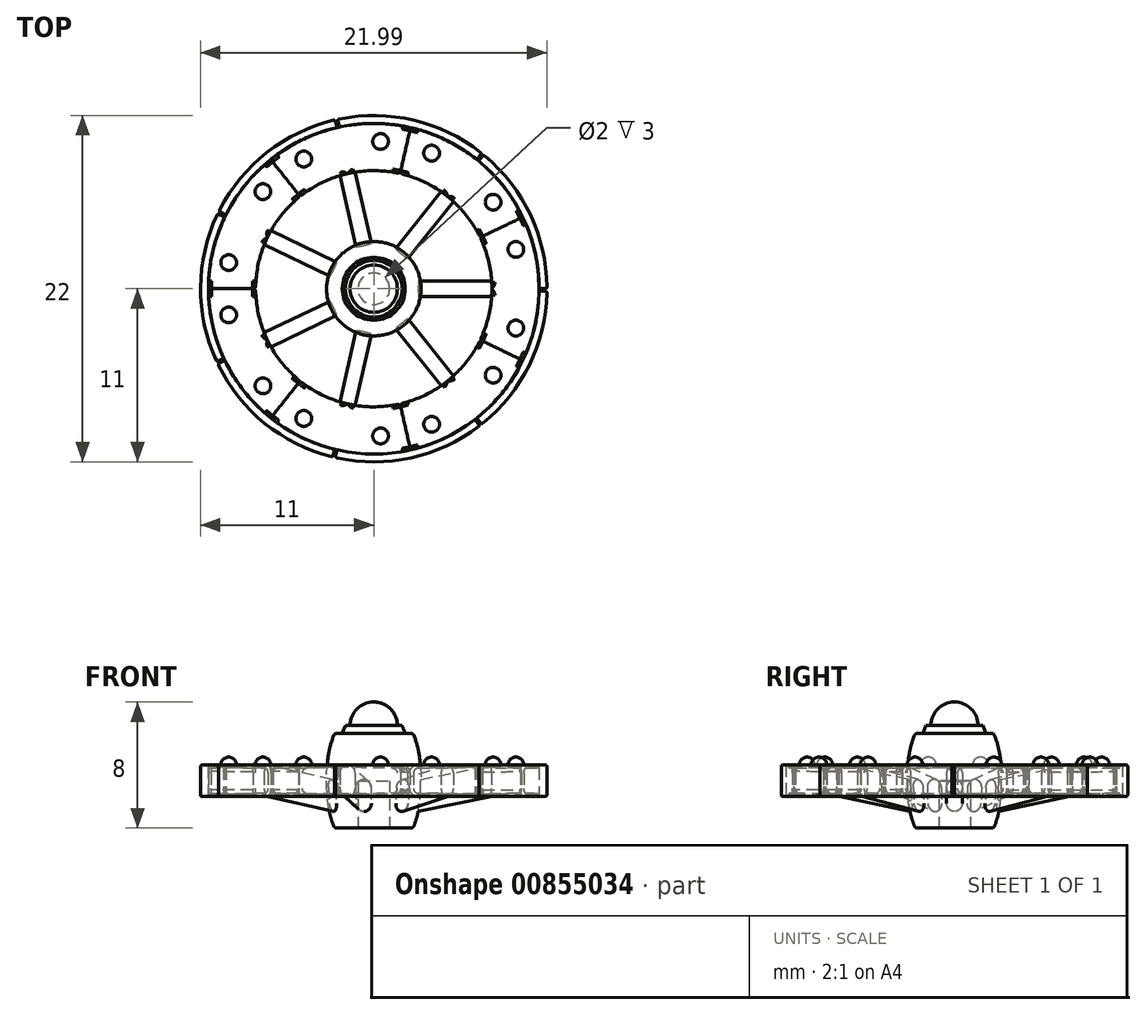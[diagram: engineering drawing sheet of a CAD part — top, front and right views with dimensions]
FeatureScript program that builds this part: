
annotation { "Feature Type Name" : "Feature", "Feature Type Description" : "" }
export const myFeature = defineFeature(function(context is Context, id is Id, definition is map)
    precondition{}
    {
        {
            var Q0;
            Q0=qCreatedBy(makeId("Front.planeOp"),FACE);
            var sketch = newSketch(context, id + "F0", { "sketchPlane" : qUnion([Q0])});
            skLineSegment(sketch, "E0", {"start": v(0, 3) * mm, "end": v(2.5, 3) * mm});
            skLineSegment(sketch, "E1", {"start": v(0, -3) * mm, "end": v(2.5, -3) * mm});
            skFitSpline(sketch, "E2", {"points": [v(2.5, 3) * mm, v(3, 0) * mm, v(2.5, -3) * mm], "startDerivative": vector(2.5, -6) * mm, "endDerivative": vector(-2.5, -6) * mm});
            skLineSegment(sketch, "E3", {"start": v(0, 3) * mm, "end": v(0, -3) * mm});
            skSolve(sketch);
        }
        {
            var Q0;
            Q0=makeQuery(id+"F0.imprint","IMPRINT",FACE,{"disambiguationData":[TD([[makeQuery(id+"F0.imprint","IMPRINT",EDGE,{"derivedFrom":sQuery(id+"F0.wireOp",EDGE,"E0")}),-1.0]])]});
            var Q1;
            Q1=sQuery(id+"F0.wireOp",EDGE,"E3");
            revolve(context, id + "F1", {"surfaceOperationType" : NewSurfaceOperationType.NEW, "entities" : qUnion([Q0]), "axis" : qUnion([Q1]), "revolveType" : RevolveType.SYMMETRIC, "angle" : 51.5 * degree});
        }
        {
            var Q0;
            Q0=qCreatedBy(makeId("Front.planeOp"),FACE);
            var sketch = newSketch(context, id + "F2", { "sketchPlane" : qUnion([Q0])});
            skLineSegment(sketch, "E4", {"start": v(2.6, -2) * mm, "end": v(7.5, -1) * mm});
            skLineSegment(sketch, "E5", {"start": v(7.5, -1) * mm, "end": v(10.5, -1) * mm});
            skLineSegment(sketch, "E6", {"start": v(10.5, -1) * mm, "end": v(10.5, 1) * mm});
            skLineSegment(sketch, "E7", {"start": v(10.5, 1) * mm, "end": v(7.5, 1) * mm});
            skLineSegment(sketch, "E8", {"start": v(7.5, 1) * mm, "end": v(2.6, 0) * mm});
            skPoint(sketch, "E9.0", {"position": v(2.5, -3) * mm});
            skFitSpline(sketch, "E10.0", {"points": [v(2.5, 3) * mm, v(2.92, 2) * mm, v(3.08, 0) * mm, v(2.92, -2) * mm, v(2.5, -3) * mm]});
            skLineSegment(sketch, "E11", {"start": v(7.5, 1) * mm, "end": v(7.5, -1) * mm});
            skLineSegment(sketch, "E12", {"start": v(2.6, 0) * mm, "end": v(2.6, -2) * mm});
            skSolve(sketch);
        }
        {
            var Q0;
            {var subQ0=sQuery(id+"F2.wireOp",EDGE,"E12");Q0=makeQuery(id+"F2.imprint","IMPRINT",FACE,{"disambiguationData":[TD([[makeQuery(id+"F2.imprint","IMPRINT",EDGE,{"derivedFrom":subQ0}),1.0]])]});}
            var Q1;
            {var subQ0=sQuery(id+"F2.wireOp",EDGE,"E11");Q1=makeQuery(id+"F2.imprint","IMPRINT",FACE,{"disambiguationData":[TD([[makeQuery(id+"F2.imprint","IMPRINT",EDGE,{"derivedFrom":subQ0}),-1.0]])]});}
            extrude(context, id + "F3", {"entities" : qUnion([Q0, Q1]), "operationType" : NewBodyOperationType.ADD, "endBound" : BoundingType.SYMMETRIC, "depth" : 1 * mm, "offsetDistance" : 25 * mm});
        }
        {
            var Q0;
            Q0=qCreatedBy(makeId("Top.planeOp"),FACE);
            var sketch = newSketch(context, id + "F4", { "sketchPlane" : qUnion([Q0])});
            skPoint(sketch, "E13.0", {"position": v(7.5, 0) * mm});
            skCircle(sketch, "E14", {"center": v(0, 0) * mm, "radius": 7.5 * mm});
            skCircle(sketch, "E15", {"center": v(0, 0) * mm, "radius": 10.5 * mm});
            skLineSegment(sketch, "E16", {"start": v(0, 0) * mm, "end": v(9.46, 4.56) * mm});
            skLineSegment(sketch, "E17", {"start": v(0, 0) * mm, "end": v(9.46, -4.56) * mm});
            skLineSegment(sketch, "E18", {"start": v(7.5, 0) * mm, "end": v(9.46, 4.56) * mm, "construction": true});
            skLineSegment(sketch, "E19", {"start": v(7.5, 0) * mm, "end": v(9.46, -4.56) * mm, "construction": true});
            skSolve(sketch);
        }
        {
            var Q0;
            {var subQ0=sQuery(id+"F4.wireOp",EDGE,"E16");var subQ1=sQuery(id+"F4.wireOp",EDGE,"E14");var subQ2=makeQuery(id+"F4.imprint","INTERSECT",VERTEX,{"derivedFrom":[subQ1,subQ0]});Q0=makeQuery(id+"F4.imprint","IMPRINT",FACE,{"disambiguationData":[TD([[makeQuery(id+"F4.imprint","IMPRINT",EDGE,{"disambiguationData":[TD([[subQ2,1.0]])],"derivedFrom":subQ1}),-1.0]])]});}
            extrude(context, id + "F5", {"entities" : qUnion([Q0]), "operationType" : NewBodyOperationType.ADD, "endBound" : BoundingType.SYMMETRIC, "depth" : 2 * mm, "offsetDistance" : 25 * mm});
        }
        {
            var Q0;
            Q0=makeQuery(id+"F5.opExtrude","CAP_EDGE",EDGE,{"disambiguationData":[OSD([sQuery(id+"F4.wireOp",EDGE,"E17")])],"isStart":false});
            var Q1;
            Q1=makeQuery(id+"F5.opExtrude","CAP_EDGE",EDGE,{"disambiguationData":[OSD([sQuery(id+"F4.wireOp",EDGE,"E17")])],"isStart":true});
            var Q2;
            Q2=makeQuery(id+"F5.opExtrude","CAP_EDGE",EDGE,{"disambiguationData":[OSD([sQuery(id+"F4.wireOp",EDGE,"E16")])],"isStart":false});
            var Q3;
            Q3=makeQuery(id+"F5.opExtrude","CAP_EDGE",EDGE,{"disambiguationData":[OSD([sQuery(id+"F4.wireOp",EDGE,"E16")])],"isStart":true});
            var Q4;
            Q4=makeQuery(id+"F3.opExtrude","CAP_EDGE",EDGE,{"disambiguationData":[OSD([sQuery(id+"F2.wireOp",EDGE,"E4")])],"isStart":false});
            var Q5;
            Q5=makeQuery(id+"F3.opExtrude","CAP_EDGE",EDGE,{"disambiguationData":[OSD([sQuery(id+"F2.wireOp",EDGE,"E4")])],"isStart":true});
            var Q6;
            Q6=makeQuery(id+"F3.opExtrude","CAP_EDGE",EDGE,{"disambiguationData":[OSD([sQuery(id+"F2.wireOp",EDGE,"E8")])],"isStart":false});
            var Q7;
            Q7=makeQuery(id+"F3.opExtrude","CAP_EDGE",EDGE,{"disambiguationData":[OSD([sQuery(id+"F2.wireOp",EDGE,"E8")])],"isStart":true});
            fillet(context, id + "F6", {"entities" : qUnion([Q0, Q1, Q2, Q3, Q4, Q5, Q6, Q7]), "radius" : .5 * mm, "tangentPropagation" : true, "allowEdgeOverflow" : false});
        }
        {
            var Q0;
            {var subQ0=sQuery(id+"F4.wireOp",EDGE,"E14");var subQ1=sQuery(id+"F4.wireOp",EDGE,"E16");Q0=makeQuery(id+"F5.boolean.opBoolean","SPLIT",EDGE,{"disambiguationData":[TD([makeQuery(id+"F5.opExtrude","SWEPT_FACE",FACE,{"disambiguationData":[OSD([subQ1])]})])],"derivedFrom":makeQuery(id+"F5.opExtrude","CAP_EDGE",EDGE,{"disambiguationData":[OSD([subQ0])],"isStart":false})});}
            var Q1;
            Q1=makeQuery(id+"F5.opExtrude","CAP_EDGE",EDGE,{"disambiguationData":[OSD([sQuery(id+"F4.wireOp",EDGE,"E15")])],"isStart":false});
            var Q2;
            Q2=makeQuery(id+"F1.opRevolve","SWEPT_EDGE",EDGE,{"disambiguationData":[OSD([sQuery(id+"F0.wireOp",EDGE,"E0"),sQuery(id+"F0.wireOp",EDGE,"E2")])]});
            var Q3;
            Q3=makeQuery(id+"F1.opRevolve","SWEPT_EDGE",EDGE,{"disambiguationData":[OSD([sQuery(id+"F0.wireOp",EDGE,"E1"),sQuery(id+"F0.wireOp",EDGE,"E2")])]});
            fillet(context, id + "F7", {"entities" : qUnion([Q0, Q1, Q2, Q3]), "radius" : .2 * mm, "tangentPropagation" : true, "allowEdgeOverflow" : false});
        }
        {
            var Q0;
            Q0=makeQuery(id+"F5.opExtrude","CAP_FACE",FACE,{"disambiguationData":[OSD([sQuery(id+"F4.wireOp",EDGE,"E14"),sQuery(id+"F4.wireOp",EDGE,"E15"),sQuery(id+"F4.wireOp",EDGE,"E16"),sQuery(id+"F4.wireOp",EDGE,"E17")])],"isStart":false});
            var sketch = newSketch(context, id + "F8", { "sketchPlane" : qUnion([Q0])});
            skCircle(sketch, "E20", {"center": v(9.02, 2.5) * mm, "radius": 0.5 * mm});
            skCircle(sketch, "E21", {"center": v(9.02, -2.5) * mm, "radius": 0.5 * mm});
            skArc(sketch, "E22", {"start": v(8.58, -3.58) * mm, "mid": v(9.42, 0) * mm, "end": v(8.58, 3.58) * mm});
            skSolve(sketch);
        }
        {
            var Q0;
            {var subQ0=sQuery(id+"F8.wireOp",EDGE,"E22");var subQ1=sQuery(id+"F8.wireOp",EDGE,"E20");var subQ2=makeQuery(id+"F8.imprint","INTERSECT",VERTEX,{"disambiguationData":[OD(0.0)],"derivedFrom":[subQ1,subQ0]});Q0=makeQuery(id+"F8.imprint","IMPRINT",FACE,{"disambiguationData":[TD([[makeQuery(id+"F8.imprint","IMPRINT",EDGE,{"disambiguationData":[TD([[subQ2,-1.0]])],"derivedFrom":subQ1}),1.0]])]});}
            var Q1;
            {var subQ0=sQuery(id+"F8.wireOp",EDGE,"E22");var subQ1=sQuery(id+"F8.wireOp",EDGE,"E20");var subQ2=makeQuery(id+"F8.imprint","INTERSECT",VERTEX,{"disambiguationData":[OD(0.0)],"derivedFrom":[subQ1,subQ0]});Q1=makeQuery(id+"F8.imprint","IMPRINT",FACE,{"disambiguationData":[TD([[makeQuery(id+"F8.imprint","IMPRINT",EDGE,{"disambiguationData":[TD([[subQ2,1.0]])],"derivedFrom":subQ1}),1.0]])]});}
            var Q2;
            {var subQ0=sQuery(id+"F8.wireOp",EDGE,"E22");var subQ1=sQuery(id+"F8.wireOp",EDGE,"E21");var subQ2=makeQuery(id+"F8.imprint","INTERSECT",VERTEX,{"disambiguationData":[OD(0.0)],"derivedFrom":[subQ1,subQ0]});Q2=makeQuery(id+"F8.imprint","IMPRINT",FACE,{"disambiguationData":[TD([[makeQuery(id+"F8.imprint","IMPRINT",EDGE,{"disambiguationData":[TD([[subQ2,-1.0]])],"derivedFrom":subQ1}),1.0]])]});}
            var Q3;
            {var subQ0=sQuery(id+"F8.wireOp",EDGE,"E22");var subQ1=sQuery(id+"F8.wireOp",EDGE,"E21");var subQ2=makeQuery(id+"F8.imprint","INTERSECT",VERTEX,{"disambiguationData":[OD(0.0)],"derivedFrom":[subQ1,subQ0]});Q3=makeQuery(id+"F8.imprint","IMPRINT",FACE,{"disambiguationData":[TD([[makeQuery(id+"F8.imprint","IMPRINT",EDGE,{"disambiguationData":[TD([[subQ2,1.0]])],"derivedFrom":subQ1}),1.0]])]});}
            extrude(context, id + "F9", {"entities" : qUnion([Q0, Q1, Q2, Q3]), "operationType" : NewBodyOperationType.ADD, "depth" : 0.5 * mm, "offsetDistance" : 25 * mm});
        }
        {
            var Q0;
            Q0=makeQuery(id+"F9.opExtrude","CAP_EDGE",EDGE,{"disambiguationData":[OSD([sQuery(id+"F8.wireOp",EDGE,"E20")])],"isStart":false});
            var Q1;
            Q1=makeQuery(id+"F9.opExtrude","CAP_EDGE",EDGE,{"disambiguationData":[OSD([sQuery(id+"F8.wireOp",EDGE,"E21")])],"isStart":false});
            fillet(context, id + "F10", {"entities" : qUnion([Q0, Q1]), "radius" : .5 * mm, "tangentPropagation" : true, "allowEdgeOverflow" : false});
        }
        {
            var Q0;
            Q0=makeQuery(id+"F3.opExtrude","SWEPT_BODY",BODY,{"disambiguationData":[OSD([sQuery(id+"F2.wireOp",EDGE,"E4"),sQuery(id+"F2.wireOp",EDGE,"E8"),sQuery(id+"F2.wireOp",EDGE,"E10.0"),sQuery(id+"F2.wireOp",EDGE,"E11")])]});
            var Q1;
            Q1=makeQuery(id+"F1.opRevolve","SWEPT_BODY",BODY,{"disambiguationData":[OSD([sQuery(id+"F0.wireOp",EDGE,"E0"),sQuery(id+"F0.wireOp",EDGE,"E1"),sQuery(id+"F0.wireOp",EDGE,"E2"),sQuery(id+"F0.wireOp",EDGE,"E3")])]});
            var Q2;
            Q2=sQuery(id+"F0.wireOp",EDGE,"E3");
            circularPattern(context, id + "F11", {"operationType" : NewBodyOperationType.ADD, "entities" : qUnion([Q0, Q1]), "axis" : qUnion([Q2]), "angle" : 360 * degree, "instanceCount" : 7, "equalSpace" : true});
        }
        {
            var Q0;
            Q0=makeQuery(id+"F5.opExtrude","CAP_FACE",FACE,{"disambiguationData":[OSD([sQuery(id+"F4.wireOp",EDGE,"E14"),sQuery(id+"F4.wireOp",EDGE,"E15"),sQuery(id+"F4.wireOp",EDGE,"E16"),sQuery(id+"F4.wireOp",EDGE,"E17")])],"isStart":false});
            var sketch = newSketch(context, id + "F12", { "sketchPlane" : qUnion([Q0])});
            skArc(sketch, "E23", {"start": v(10.5, 0) * mm, "mid": v(9.5, 4.49) * mm, "end": v(6.66, 8.1) * mm});
            skLineSegment(sketch, "E24", {"start": v(6.66, 8.1) * mm, "end": v(6.92, 8.42) * mm});
            skLineSegment(sketch, "E25", {"start": v(10.5, 0) * mm, "end": v(10.9, 0) * mm});
            skArc(sketch, "E26", {"start": v(11, 0.1) * mm, "mid": v(9.95, 4.7) * mm, "end": v(7.06, 8.43) * mm});
            skLineSegment(sketch, "E27", {"start": v(0, 0) * mm, "end": v(9.95, 4.7) * mm, "construction": true});
            skPoint(sketch, "E28.visualSharp", {"position": v(6.98, 8.5) * mm});
            skArc(sketch, "E28.filletArc", {"start": v(7.06, 8.43) * mm, "mid": v(6.99, 8.45) * mm, "end": v(6.92, 8.42) * mm});
            skPoint(sketch, "E29.visualSharp", {"position": v(11, 0) * mm});
            skArc(sketch, "E29.filletArc", {"start": v(10.9, 0) * mm, "mid": v(10.97, 0.03) * mm, "end": v(11, 0.1) * mm});
            skSolve(sketch);
        }
        {
            var Q0;
            Q0=makeQuery(id+"F12.imprint","IMPRINT",FACE,{"disambiguationData":[TD([[makeQuery(id+"F12.imprint","IMPRINT",EDGE,{"derivedFrom":sQuery(id+"F12.wireOp",EDGE,"E23")}),-1.0]])]});
            extrude(context, id + "F13", {"entities" : qUnion([Q0]), "oppositeDirection" : true, "depth" : 2 * mm, "offsetDistance" : 25 * mm});
        }
        {
            var Q0;
            Q0=makeQuery(id+"F13.opExtrude","CAP_EDGE",EDGE,{"disambiguationData":[OSD([sQuery(id+"F12.wireOp",EDGE,"E26")])],"isStart":true});
            var Q1;
            Q1=makeQuery(id+"F13.opExtrude","CAP_EDGE",EDGE,{"disambiguationData":[OSD([sQuery(id+"F12.wireOp",EDGE,"E26")])],"isStart":false});
            fillet(context, id + "F14", {"entities" : qUnion([Q0, Q1]), "radius" : .1 * mm, "tangentPropagation" : true, "allowEdgeOverflow" : false});
        }
        {
            var Q0;
            Q0=makeQuery(id+"F13.opExtrude","SWEPT_BODY",BODY,{"disambiguationData":[OSD([sQuery(id+"F12.wireOp",EDGE,"E23"),sQuery(id+"F12.wireOp",EDGE,"E24"),sQuery(id+"F12.wireOp",EDGE,"E25"),sQuery(id+"F12.wireOp",EDGE,"E26")])]});
            var Q1;
            Q1=sQuery(id+"F0.wireOp",EDGE,"E3");
            circularPattern(context, id + "F15", {"operationType" : NewBodyOperationType.ADD, "entities" : qUnion([Q0]), "axis" : qUnion([Q1]), "angle" : 360 * degree, "instanceCount" : 7, "equalSpace" : true});
        }
        {
            var Q0;
            Q0=makeQuery(id+"F1.opRevolve","SWEPT_FACE",FACE,{"disambiguationData":[OSD([sQuery(id+"F0.wireOp",EDGE,"E0")])]});
            var sketch = newSketch(context, id + "F16", { "sketchPlane" : qUnion([Q0])});
            skCircle(sketch, "E30", {"center": v(0, 0) * mm, "radius": 2 * mm});
            skSolve(sketch);
        }
        {
            var Q0;
            Q0=makeQuery(id+"F16.imprint","IMPRINT",FACE,{"disambiguationData":[TD([[makeQuery(id+"F16.imprint","IMPRINT",EDGE,{"derivedFrom":sQuery(id+"F16.wireOp",EDGE,"E30")}),1.0]])]});
            extrude(context, id + "F17", {"entities" : qUnion([Q0]), "operationType" : NewBodyOperationType.ADD, "depth" : .5 * mm, "offsetDistance" : 25 * mm});
        }
        {
            var Q0;
            Q0=makeQuery(id+"F17.opExtrude","CAP_EDGE",EDGE,{"disambiguationData":[OSD([sQuery(id+"F16.wireOp",EDGE,"E30")])],"isStart":false});
            chamfer(context, id + "F18", {"entities" : qUnion([Q0]), "chamferType" : ChamferType.TWO_OFFSETS, "width1" : 0.2 * mm, "oppositeDirection" : false, "width2" : .5 * mm, "tangentPropagation" : true});
        }
        {
            var Q0;
            Q0=makeQuery(id+"F17.opExtrude","CAP_FACE",FACE,{"disambiguationData":[OSD([sQuery(id+"F16.wireOp",EDGE,"E30")])],"isStart":false});
            var sketch = newSketch(context, id + "F19", { "sketchPlane" : qUnion([Q0])});
            skCircle(sketch, "E31", {"center": v(0, 0) * mm, "radius": 1.5 * mm});
            skSolve(sketch);
        }
        {
            var Q0;
            Q0=makeQuery(id+"F19.imprint","IMPRINT",FACE,{"disambiguationData":[TD([[makeQuery(id+"F19.imprint","IMPRINT",EDGE,{"derivedFrom":sQuery(id+"F19.wireOp",EDGE,"E31")}),1.0]])]});
            extrude(context, id + "F20", {"entities" : qUnion([Q0]), "operationType" : NewBodyOperationType.ADD, "depth" : 1.5 * mm, "offsetDistance" : 25 * mm});
        }
        {
            var Q0;
            Q0=makeQuery(id+"F20.opExtrude","CAP_EDGE",EDGE,{"disambiguationData":[OSD([sQuery(id+"F19.wireOp",EDGE,"E31")])],"isStart":false});
            fillet(context, id + "F21", {"entities" : qUnion([Q0]), "radius" : 1.5 * mm, "tangentPropagation" : true, "allowEdgeOverflow" : false});
        }
        {
            var Q0;
            Q0=makeQuery(id+"F1.opRevolve","SWEPT_FACE",FACE,{"disambiguationData":[OSD([sQuery(id+"F0.wireOp",EDGE,"E1")])]});
            var sketch = newSketch(context, id + "F22", { "sketchPlane" : qUnion([Q0])});
            skCircle(sketch, "E32", {"center": v(0, 0) * mm, "radius": 1 * mm});
            skSolve(sketch);
        }
        {
            var Q0;
            Q0=makeQuery(id+"F22.imprint","IMPRINT",FACE,{"disambiguationData":[TD([[makeQuery(id+"F22.imprint","IMPRINT",EDGE,{"derivedFrom":sQuery(id+"F22.wireOp",EDGE,"E32")}),1.0]])]});
            extrude(context, id + "F23", {"entities" : qUnion([Q0]), "operationType" : NewBodyOperationType.REMOVE, "oppositeDirection" : true, "depth" : 3 * mm, "offsetDistance" : 25 * mm});
        }
    });
